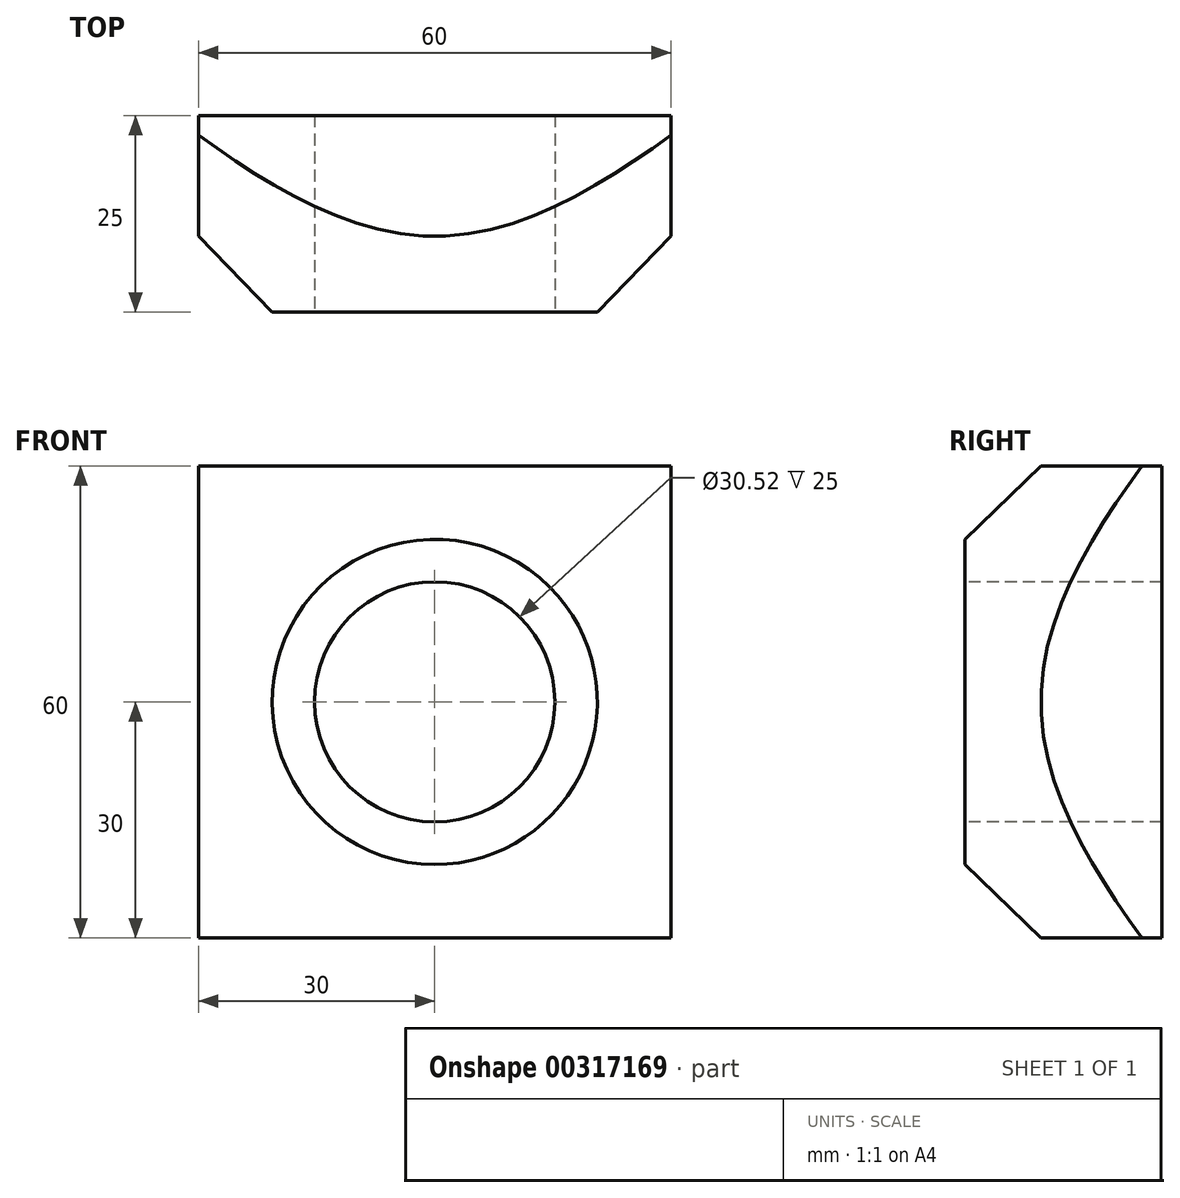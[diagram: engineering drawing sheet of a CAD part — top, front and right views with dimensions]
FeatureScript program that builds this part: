
annotation { "Feature Type Name" : "Feature", "Feature Type Description" : "" }
export const myFeature = defineFeature(function(context is Context, id is Id, definition is map)
    precondition{}
    {
        {
            var Q0;
            Q0=qCreatedBy(makeId("Front.planeOp"),FACE);
            var sketch = newSketch(context, id + "F0", { "sketchPlane" : qUnion([Q0])});
            skLineSegment(sketch, "E0.bottom", {"start": v(30, 30) * mm, "end": v(-30, 30) * mm});
            skLineSegment(sketch, "E0.top", {"start": v(30, -30) * mm, "end": v(-30, -30) * mm});
            skLineSegment(sketch, "E0.left", {"start": v(30, 30) * mm, "end": v(30, -30) * mm});
            skLineSegment(sketch, "E0.right", {"start": v(-30, 30) * mm, "end": v(-30, -30) * mm});
            skPoint(sketch, "E0.middle", {"position": v(0, 0) * mm});
            skSolve(sketch);
        }
        {
            var Q0;
            Q0 = qSketchRegion(id + "F0", true);
            extrude(context, id + "F1", {"entities" : qUnion([Q0]), "depth" : 25 * mm});
        }
        {
            var Q0;
            Q0=qCreatedBy(makeId("Front.planeOp"),FACE);
            var sketch = newSketch(context, id + "F2", { "sketchPlane" : qUnion([Q0])});
            skCircle(sketch, "E1", {"center": v(0, 0) * mm, "radius": 44.84 * mm});
            skSolve(sketch);
        }
        {
            var Q0;
            Q0=makeQuery(id+"F1.opExtrude","CAP_FACE",FACE,{"disambiguationData":[OSD([sQuery(id+"F0.wireOp",EDGE,"E0.bottom"),sQuery(id+"F0.wireOp",EDGE,"E0.top"),sQuery(id+"F0.wireOp",EDGE,"E0.left"),sQuery(id+"F0.wireOp",EDGE,"E0.right")])],"isStart":false});
            var sketch = newSketch(context, id + "F3", { "sketchPlane" : qUnion([Q0])});
            skCircle(sketch, "E2", {"center": v(0, 0) * mm, "radius": 20.66 * mm});
            skSolve(sketch);
        }
        {
            var Q1;
            Q1=makeQuery(id+"F2.imprint","IMPRINT",FACE,{"disambiguationData":[TD([[makeQuery(id+"F2.imprint","IMPRINT",EDGE,{"derivedFrom":sQuery(id+"F2.wireOp",EDGE,"E1")}),1.0]])]});
            var Q2;
            Q2=makeQuery(id+"F3.imprint","IMPRINT",FACE,{"disambiguationData":[TD([[makeQuery(id+"F3.imprint","IMPRINT",EDGE,{"derivedFrom":sQuery(id+"F3.wireOp",EDGE,"E2")}),1.0]])]});
            loft(context, id + "F4", {"operationType" : NewBodyOperationType.INTERSECT, "sheetProfilesArray" : [{ "sheetProfileEntities" : qUnion([Q1]) }, { "sheetProfileEntities" : qUnion([Q2]) }]});
        }
        {
            var Q0;
            Q0=makeQuery(id+"F1.opExtrude","CAP_FACE",FACE,{"disambiguationData":[OSD([sQuery(id+"F0.wireOp",EDGE,"E0.bottom"),sQuery(id+"F0.wireOp",EDGE,"E0.top"),sQuery(id+"F0.wireOp",EDGE,"E0.left"),sQuery(id+"F0.wireOp",EDGE,"E0.right")])],"isStart":false});
            var sketch = newSketch(context, id + "F5", { "sketchPlane" : qUnion([Q0])});
            skCircle(sketch, "E3", {"center": v(0, 0) * mm, "radius": 15.26 * mm});
            skSolve(sketch);
        }
        {
            var Q0;
            Q0 = qSketchRegion(id + "F5", true);
            extrude(context, id + "F6", {"entities" : qUnion([Q0]), "operationType" : NewBodyOperationType.REMOVE, "oppositeDirection" : true, "depth" : 30 * mm});
        }
    });
